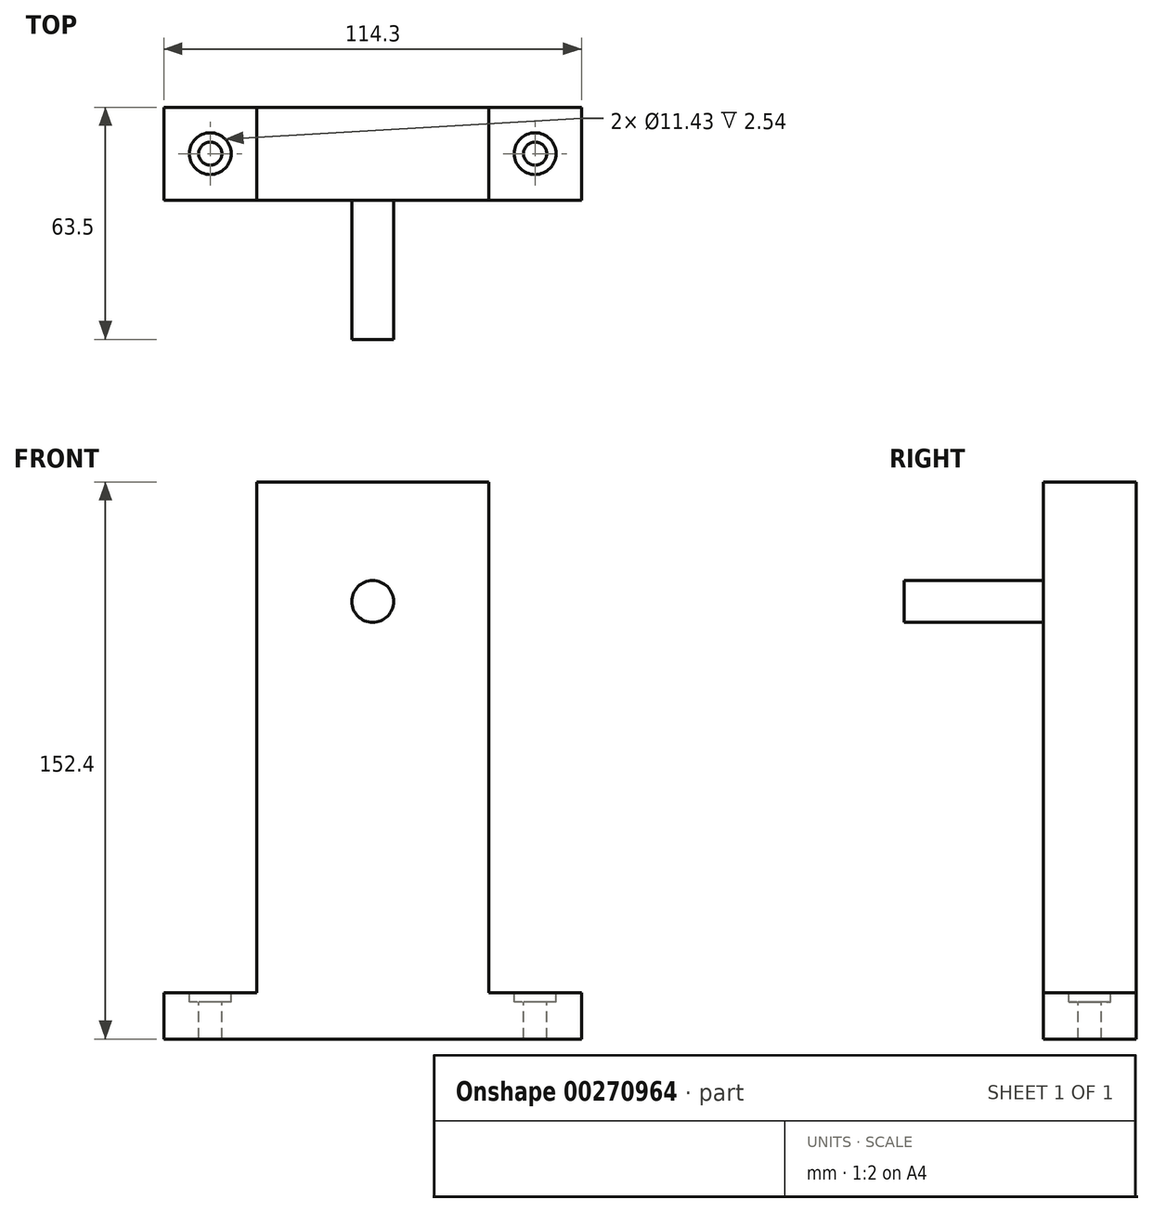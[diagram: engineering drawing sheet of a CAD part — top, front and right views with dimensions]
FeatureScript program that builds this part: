
annotation { "Feature Type Name" : "Feature", "Feature Type Description" : "" }
export const myFeature = defineFeature(function(context is Context, id is Id, definition is map)
    precondition{}
    {
        {
            var Q0;
            Q0=qCreatedBy(makeId("Front.planeOp"),FACE);
            var sketch = newSketch(context, id + "F0", { "sketchPlane" : qUnion([Q0])});
            skLineSegment(sketch, "E0", {"start": v(0, 0) * mm, "end": v(0, 12.7) * mm});
            skLineSegment(sketch, "E1", {"start": v(0, 0) * mm, "end": v(-114.3, 0) * mm});
            skLineSegment(sketch, "E2", {"start": v(-114.3, 0) * mm, "end": v(-114.3, 12.7) * mm});
            skLineSegment(sketch, "E3", {"start": v(-114.3, 12.7) * mm, "end": v(-88.9, 12.7) * mm});
            skLineSegment(sketch, "E4", {"start": v(-88.9, 12.7) * mm, "end": v(-88.9, 152.4) * mm});
            skLineSegment(sketch, "E5", {"start": v(-88.9, 152.4) * mm, "end": v(-25.4, 152.4) * mm});
            skLineSegment(sketch, "E6", {"start": v(-25.4, 152.4) * mm, "end": v(-25.4, 12.7) * mm});
            skLineSegment(sketch, "E7", {"start": v(-25.4, 12.7) * mm, "end": v(0, 12.7) * mm});
            skPoint(sketch, "E8.orphan", {"position": v(-88.9, 0) * mm});
            skSolve(sketch);
        }
        {
            var Q0;
            Q0 = qSketchRegion(id + "F0", true);
            extrude(context, id + "F1", {"entities" : qUnion([Q0]), "depth" : 25.4 * mm});
        }
        {
            var Q0;
            Q0=makeQuery(id+"F1.opExtrude","CAP_FACE",FACE,{"disambiguationData":[OSD([sQuery(id+"F0.wireOp",EDGE,"E0"),sQuery(id+"F0.wireOp",EDGE,"E1"),sQuery(id+"F0.wireOp",EDGE,"E2"),sQuery(id+"F0.wireOp",EDGE,"E3"),sQuery(id+"F0.wireOp",EDGE,"E4"),sQuery(id+"F0.wireOp",EDGE,"E5"),sQuery(id+"F0.wireOp",EDGE,"E6"),sQuery(id+"F0.wireOp",EDGE,"E7")])],"isStart":false});
            var sketch = newSketch(context, id + "F2", { "sketchPlane" : qUnion([Q0])});
            skLineSegment(sketch, "E9.0.0", {"start": v(0, 12.7) * mm, "end": v(-25.4, 12.7) * mm});
            skLineSegment(sketch, "E9.0.1", {"start": v(-25.4, 12.7) * mm, "end": v(-25.4, 152.4) * mm});
            skLineSegment(sketch, "E9.0.2", {"start": v(-25.4, 152.4) * mm, "end": v(-88.9, 152.4) * mm});
            skLineSegment(sketch, "E9.0.3", {"start": v(-88.9, 152.4) * mm, "end": v(-88.9, 12.7) * mm});
            skLineSegment(sketch, "E9.0.4", {"start": v(-88.9, 12.7) * mm, "end": v(-114.3, 12.7) * mm});
            skLineSegment(sketch, "E9.0.5", {"start": v(-114.3, 12.7) * mm, "end": v(-114.3, 0) * mm});
            skLineSegment(sketch, "E9.0.6", {"start": v(-114.3, 0) * mm, "end": v(0, 0) * mm});
            skLineSegment(sketch, "E9.0.7", {"start": v(0, 0) * mm, "end": v(0, 12.7) * mm});
            skLineSegment(sketch, "E10", {"start": v(-57.15, 152.4) * mm, "end": v(-57.15, 119.68) * mm});
            skCircle(sketch, "E11", {"center": v(-57.15, 119.68) * mm, "radius": 5.72 * mm});
            skSolve(sketch);
        }
        {
            var Q0;
            Q0=makeQuery(id+"F2.imprint","IMPRINT",FACE,{"disambiguationData":[TD([[makeQuery(id+"F2.imprint","IMPRINT",EDGE,{"derivedFrom":sQuery(id+"F2.wireOp",EDGE,"E11")}),1.0]])]});
            extrude(context, id + "F3", {"entities" : qUnion([Q0]), "operationType" : NewBodyOperationType.ADD, "depth" : 38.1 * mm});
        }
        {
            var Q0;
            Q0=makeQuery(id+"F1.opExtrude","SWEPT_FACE",FACE,{"disambiguationData":[OSD([sQuery(id+"F0.wireOp",EDGE,"E3")])]});
            var sketch = newSketch(context, id + "F4", { "sketchPlane" : qUnion([Q0])});
            skLineSegment(sketch, "E12", {"start": v(-114.3, -12.7) * mm, "end": v(-88.9, -12.7) * mm});
            skLineSegment(sketch, "E13", {"start": v(-101.6, 0) * mm, "end": v(-101.6, -25.4) * mm});
            skLineSegment(sketch, "E14.0", {"start": v(-25.4, -25.4) * mm, "end": v(0, -25.4) * mm});
            skLineSegment(sketch, "E15", {"start": v(-12.7, -25.4) * mm, "end": v(-12.7, 0) * mm});
            skLineSegment(sketch, "E16.0", {"start": v(0, -25.4) * mm, "end": v(0, 0) * mm});
            skLineSegment(sketch, "E17.0", {"start": v(-25.4, -25.4) * mm, "end": v(-25.4, 0) * mm});
            skLineSegment(sketch, "E18", {"start": v(0, -12.7) * mm, "end": v(-25.4, -12.7) * mm});
            skPoint(sketch, "E19", {"position": v(-12.7, -12.7) * mm});
            skPoint(sketch, "E20", {"position": v(-101.6, -12.7) * mm});
            skSolve(sketch);
        }
        {
            var Q0;
            Q0=sQuery(id+"F4.wireOp",VERTEX,"E20");
            var Q1;
            Q1=sQuery(id+"F4.wireOp",VERTEX,"E19");
            var Q2;
            Q2=makeQuery(id+"F1.opExtrude","SWEPT_BODY",BODY,{"disambiguationData":[OSD([sQuery(id+"F0.wireOp",EDGE,"E0"),sQuery(id+"F0.wireOp",EDGE,"E1"),sQuery(id+"F0.wireOp",EDGE,"E2"),sQuery(id+"F0.wireOp",EDGE,"E3"),sQuery(id+"F0.wireOp",EDGE,"E4"),sQuery(id+"F0.wireOp",EDGE,"E5"),sQuery(id+"F0.wireOp",EDGE,"E6"),sQuery(id+"F0.wireOp",EDGE,"E7")])]});
            hole(context, id + "F5", {"style" : HoleStyle.C_BORE, "endStyle" : HoleEndStyle.THROUGH, "holeDiameter" : 6.35 * mm, "cBoreDiameter" : 11.43 * mm, "cBoreDepth" : 2.54 * mm, "tappedDepth" : 12.7 * mm, "tapClearance" : 3, "locations" : qUnion([Q0, Q1]), "scope" : qUnion([Q2])});
        }
    });
